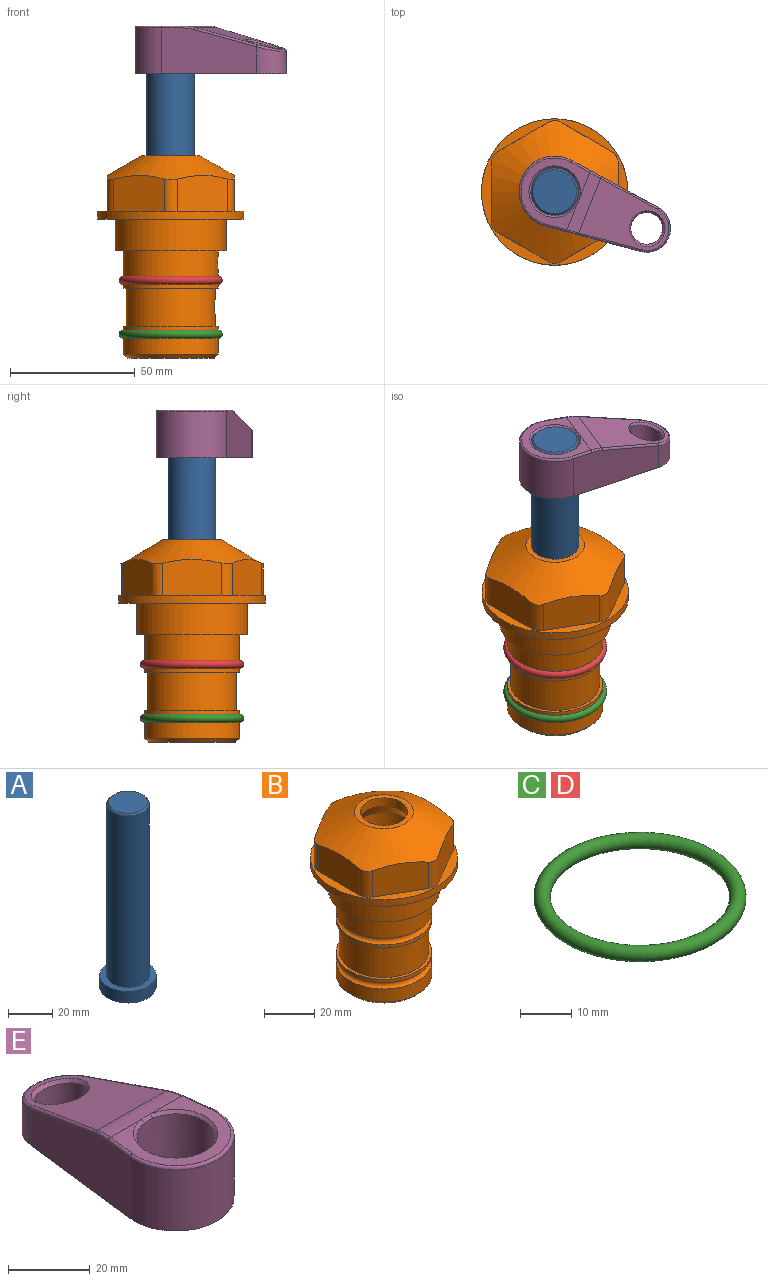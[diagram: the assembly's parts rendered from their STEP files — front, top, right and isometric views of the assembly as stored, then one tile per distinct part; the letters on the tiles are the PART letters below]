
ASSEMBLY  parts=5 mates=4
PART A: 6 faces, bbox 25.4x25.4x101.6 mm
  f0: plane 17.46x17.46mm, normal (0,0,1), area 239.5mm2, adj f5
  f1: plane 25.4x25.4mm, normal (0,0,-1), area 506.7mm2, adj f2
  f2: cylinder r=12.7mm len=25.4mm, axis (0,0,1), area 506.7mm2, adj f1,f3
  f3: plane 25.4x25.4mm, normal (0,0,1), area 221.7mm2, adj f2,f4
  f4: cylinder r=9.53mm len=94.46mm, axis (0,0,1), area 5653mm2, adj f3,f5
  f5: cone r=8.73mm half-angle=45deg, axis (0,0,-1), area 64.4mm2, adj f0,f4
PART B: 36 faces, bbox 58.7x58.7x81 mm
  f0: cylinder r=17.78mm len=35.56mm, axis (0,0,1), area 1670.8mm2, adj f23,f24,f31
  f1: cylinder r=19.05mm len=38.1mm, axis (0,0,1), area 1191.9mm2, adj f26,f27,f30
  f2: plane 58.66x58.66mm, normal (0,0,-1), area 1150.6mm2, adj f3,f28
  f3: cylinder r=29.33mm len=58.66mm, axis (0,0,-1), area 585.1mm2, adj f2,f4
  f4: plane 58.66x58.66mm, normal (0,0,1), area 475.9mm2, adj f3,f5,f6,f7,f8,f9,f10,f11
  f5: plane 20.32x14.34mm, normal (-0.5,0.87,0), area 324.4mm2, adj f4,f15,f16,f17
  f6: plane 20.32x14.34mm, normal (0.5,0.87,0), area 324.4mm2, adj f4,f14,f15,f17
  f7: plane 23.48x14.34mm, normal (1,0,0), area 324.4mm2, adj f4,f13,f14,f17
  f8: plane 20.32x14.34mm, normal (0.5,-0.87,0), area 324.4mm2, adj f4,f12,f13,f17
  f9: plane 20.32x14.34mm, normal (-0.5,-0.87,0), area 324.4mm2, adj f4,f11,f12,f17
  f10: plane 23.48x14.34mm, normal (-1,0,0), area 324.4mm2, adj f4,f11,f16,f17
  f11: cylinder r=5.08mm len=12.85mm, axis (0,0,-1), area 67.2mm2, adj f4,f9,f10,f17
  f12: cylinder r=5.08mm len=12.85mm, axis (0,0,-1), area 67.2mm2, adj f4,f8,f9,f17
  f13: cylinder r=5.08mm len=12.85mm, axis (0,0,-1), area 67.2mm2, adj f4,f7,f8,f17
  f14: cylinder r=5.08mm len=12.85mm, axis (0,0,-1), area 67.2mm2, adj f4,f6,f7,f17
  f15: cylinder r=5.08mm len=12.85mm, axis (0,0,-1), area 67.2mm2, adj f4,f5,f6,f17
  f16: cylinder r=5.08mm len=12.85mm, axis (0,0,-1), area 67.2mm2, adj f4,f5,f10,f17
  f17: cone r=11.73mm half-angle=60deg, axis (0,0,-1), area 2071.8mm2, adj f5,f6,f7,f8,f9,f10,f11,f12
  f18: plane 23.46x23.46mm, normal (0,0,1), area 147.4mm2, adj f17,f35
  f19: plane 34.93x34.93mm, normal (0,0,-1), area 958mm2, adj f29
  f20: cylinder r=19.05mm len=38.1mm, axis (0,0,1), area 760.1mm2, adj f21,f29
  f21: torus R=19.05mm, axis (0,0,1), area 565.3mm2, adj f20,f22
  f22: cylinder r=19.05mm len=38.1mm, axis (0,0,1), area 190mm2, adj f21,f23
  f23: plane 38.1x38.1mm, normal (0,0,1), area 146.9mm2, adj f0,f22
  f24: plane 38.1x38.1mm, normal (0,0,-1), area 146.9mm2, adj f0,f25
  f25: cylinder r=19.05mm len=38.1mm, axis (0,0,1), area 190mm2, adj f24,f26
  f26: torus R=19.05mm, axis (0,0,1), area 565.3mm2, adj f1,f25
  f27: plane 44.45x44.45mm, normal (0,0,-1), area 411.7mm2, adj f1,f28
  f28: cylinder r=22.23mm len=44.45mm, axis (0,0,1), area 1773.5mm2, adj f2,f27
  f29: cone r=19.05mm half-angle=45deg, axis (0,0,1), area 257.5mm2, adj f19,f20
  f30: cylinder r=3.17mm len=6.75mm, axis (-1,0,0), area 128mm2, adj f1,f33
  f31: cylinder r=3.17mm len=6.35mm, axis (-1,0,0), area 102.5mm2, adj f0,f33
  f32: plane 25.4x25.4mm, normal (0,0,1), area 506.7mm2, adj f33
  f33: cylinder r=12.7mm len=66.42mm, axis (0,0,-1), area 5236.2mm2, adj f30,f31,f32,f34
  f34: cone r=9.53mm half-angle=30deg, axis (0,0,-1), area 443.4mm2, adj f33,f35
  f35: cylinder r=9.53mm len=19.05mm, axis (0,0,-1), area 240.9mm2, adj f18,f34
PART C: 1 faces, bbox 44.7x44.7x3.2 mm
  f0: torus R=19.05mm, axis (0,0,1), area 1193.9mm2
PART D: same geometry as C
PART E: 31 faces, bbox 31.7x65.5x19.8 mm
  f0: plane 39.12x18.26mm, normal (0.99,0.12,0), area 612.2mm2, adj f1,f4,f7,f11,f13,f15
  f1: cylinder r=9.53mm len=18.91mm, axis (0,0,-1), area 296.1mm2, adj f0,f2,f7,f17
  f2: plane 39.12x18.26mm, normal (-0.99,0.12,0), area 612.2mm2, adj f1,f4,f7,f12,f14,f16
  f3: cylinder r=6.35mm len=12.7mm, axis (0,0,-1), area 362.4mm2, adj f7,f18
  f4: cylinder r=14.29mm len=28.58mm, axis (0,0,-1), area 882.2mm2, adj f0,f2,f7,f10
  f5: cylinder r=9.53mm len=19.05mm, axis (0,0,-1), area 1092.6mm2, adj f7,f19,f20
  f6: plane 26.99x23.69mm, normal (0,0,1), area 216.2mm2, adj f9,f10,f11,f12,f19
  f7: plane 63.5x28.58mm, normal (0,0,-1), area 661.8mm2, adj f0,f1,f2,f3,f4,f5,f22,f23
  f8: plane 33.52x23.6mm, normal (0,0.26,0.97), area 486mm2, adj f9,f15,f16,f17,f18
  f9: cylinder r=19.05mm len=24.72mm, axis (1,0,0), area 120.4mm2, adj f6,f8,f13,f14,f20
  f10: torus R=13.49mm, axis (0,0,1), area 59mm2, adj f4,f6,f11,f12
  f11: cylinder r=0.79mm len=8.67mm, axis (0.12,-0.99,0), area 10.8mm2, adj f0,f6,f10,f13
  f12: cylinder r=0.79mm len=8.67mm, axis (0.12,0.99,0), area 10.8mm2, adj f2,f6,f10,f14
  f13: bspline ~4.95x1.42mm, area 6.1mm2, adj f0,f9,f11,f15
  f14: bspline ~4.95x1.42mm, area 6.1mm2, adj f2,f9,f12,f16
  f15: cylinder r=0.79mm len=25.95mm, axis (0.12,-0.96,0.26), area 32.9mm2, adj f0,f8,f13,f17
  f16: cylinder r=0.79mm len=25.95mm, axis (0.12,0.96,-0.26), area 32.9mm2, adj f2,f8,f14,f17
  f17: bspline ~18.91x8.38mm, area 30mm2, adj f1,f8,f15,f16
  f18: bspline ~14.29x14.29mm, area 48.3mm2, adj f3,f8
  f19: cone r=9.53mm half-angle=45deg, axis (0,0,1), area 66.5mm2, adj f5,f6,f20
  f20: bspline ~3.22x0.96mm, area 3.5mm2, adj f5,f9,f19
  f21: plane 2.75x2.72mm, normal (0,0,-1), area 2.9mm2, adj f23,f25,f28
  f22: plane 23.05x15.88mm, normal (-0.99,-0.12,0), area 323.6mm2, adj f7,f25,f26,f27,f28,f29
  f23: plane 23.05x15.88mm, normal (0.99,-0.12,0), area 323.6mm2, adj f7,f21,f25,f27,f28,f30
  f24: cylinder r=9.53mm len=10.69mm, axis (0,0,-1), area 114.7mm2, adj f7,f27,f29,f30
  f25: cylinder r=12.7mm len=20.59mm, axis (0,0,-1), area 381.1mm2, adj f7,f21,f22,f23,f26,f28
  f26: plane 2.75x2.72mm, normal (0,0,-1), area 2.9mm2, adj f22,f25,f28
  f27: plane 19.72x18.37mm, normal (0,-0.26,-0.97), area 291.8mm2, adj f22,f23,f24,f28,f29,f30
  f28: cylinder r=15.88mm len=19.92mm, axis (1,0,0), area 54.8mm2, adj f21,f22,f23,f25,f26,f27
  f29: cylinder r=1.59mm len=11mm, axis (0,0,-1), area 34.7mm2, adj f7,f22,f24,f27
  f30: cylinder r=1.59mm len=11mm, axis (0,0,-1), area 34.7mm2, adj f7,f23,f24,f27
PLACE A rot(axis=(0,0,-1),111.7deg) t=(0,0,13.87)mm
PLACE B at identity fixed
PLACE C t=(0,0,-21.59)mm
PLACE D at identity
PLACE E rot(axis=(0,0,-1),111.7deg) t=(0,0,13.87)mm
MATE fastened C.f0 <-> B.f0  axis (0,0,1) through (0,0,-46.1)mm
MATE fastened E.f4 <-> A.f2  axis (0,0,1) through (0,0,77.37)mm
MATE fastened D.f0 <-> B.f0  axis (0,0,1) through (0,0,-24.51)mm
MATE cylindrical B.f0 <-> A.f2  axis (0,0,-1) through (0,0,21.37)mm
